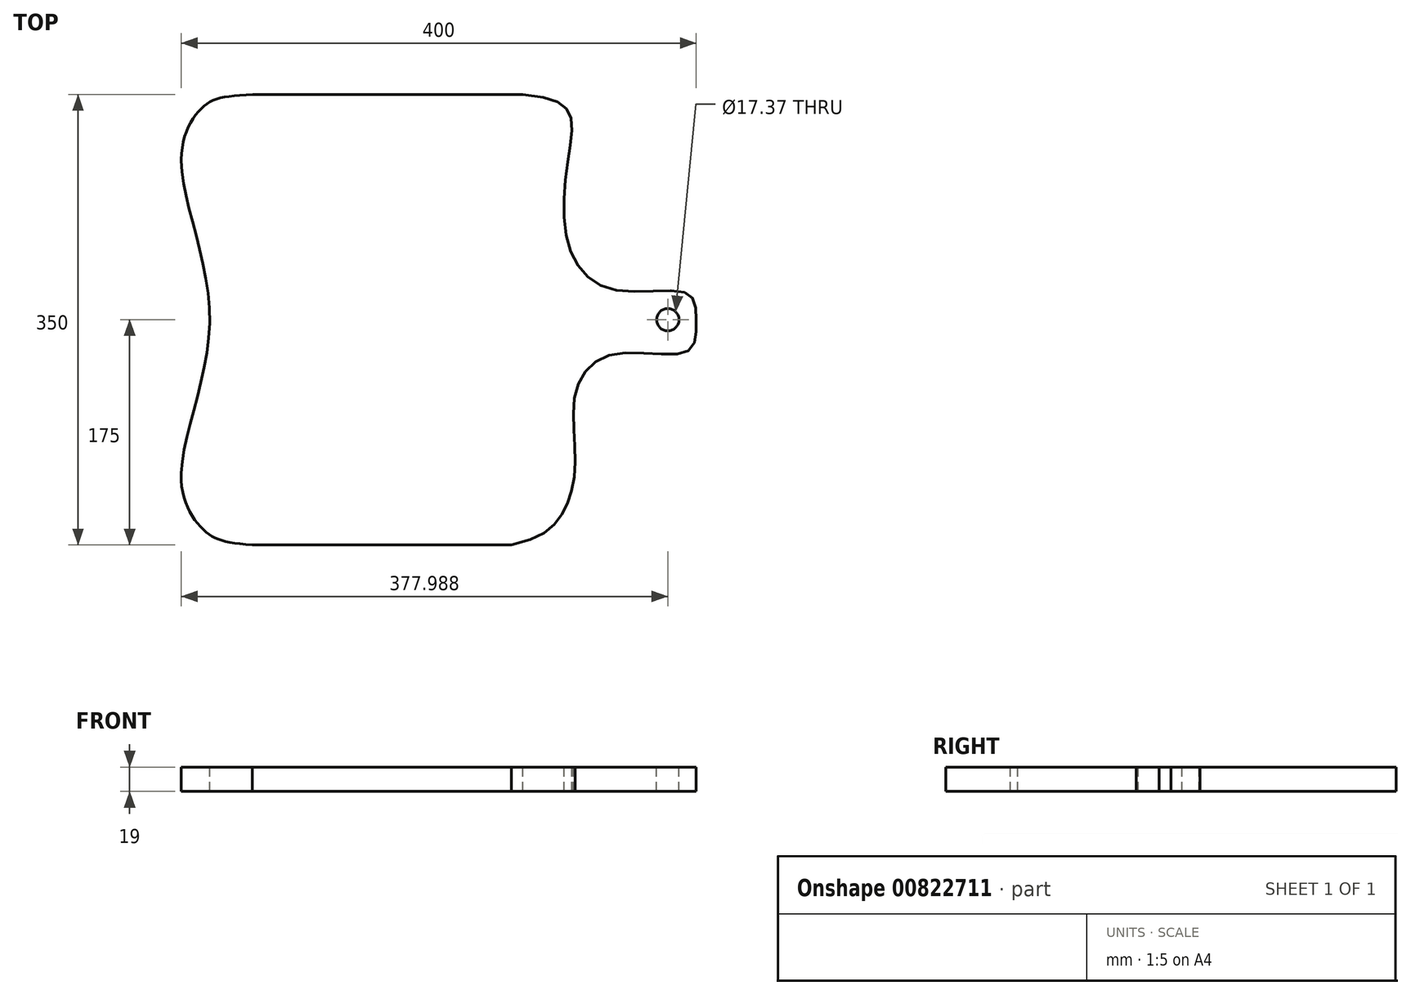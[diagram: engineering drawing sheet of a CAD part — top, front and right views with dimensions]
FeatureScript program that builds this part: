
annotation { "Feature Type Name" : "Feature", "Feature Type Description" : "" }
export const myFeature = defineFeature(function(context is Context, id is Id, definition is map)
    precondition{}
    {
        {
            var Q0;
            Q0=qCreatedBy(makeId("Top.planeOp"),FACE);
            var sketch = newSketch(context, id + "F0", { "sketchPlane" : qUnion([Q0])});
            skLineSegment(sketch, "E0.bottom", {"start": v(200, -175) * mm, "end": v(-200, -175) * mm});
            skLineSegment(sketch, "E0.top", {"start": v(200, 175) * mm, "end": v(-200, 175) * mm});
            skLineSegment(sketch, "E0.left", {"start": v(200, -175) * mm, "end": v(200, 175) * mm});
            skLineSegment(sketch, "E0.right", {"start": v(-200, -175) * mm, "end": v(-200, 175) * mm});
            skPoint(sketch, "E0.middle", {"position": v(0, 0) * mm});
            skSolve(sketch);
        }
        {
            var Q0;
            Q0 = qSketchRegion(id + "F0", true);
            extrude(context, id + "F1", {"entities" : qUnion([Q0]), "depth" : 19 * mm, "offsetDistance" : 25 * mm});
        }
        {
            var Q0;
            Q0=makeQuery(id+"F1.opExtrude","CAP_FACE",FACE,{"disambiguationData":[OSD([sQuery(id+"F0.wireOp",EDGE,"E0.bottom"),sQuery(id+"F0.wireOp",EDGE,"E0.top"),sQuery(id+"F0.wireOp",EDGE,"E0.left"),sQuery(id+"F0.wireOp",EDGE,"E0.right")])],"isStart":false});
            var sketch = newSketch(context, id + "F2", { "sketchPlane" : qUnion([Q0])});
            skFitSpline(sketch, "E1", {"points": [v(-144.39, 175) * mm, v(-182.7, 165.66) * mm, v(-200, 124.44) * mm, v(-177.97, 0) * mm, v(-200, -124.84) * mm, v(-180.58, -165.08) * mm, v(-144.98, -175) * mm, v(56.37, -175) * mm, v(96.18, -150.44) * mm, v(106.15, -110.63) * mm, v(106.57, -55.5) * mm, v(137.18, -26.5) * mm, v(193.56, -24.36) * mm, v(200, 0) * mm, v(193.56, 20.21) * mm, v(138.25, 22.9) * mm, v(103.09, 51.7) * mm, v(99.33, 116.14) * mm, v(101.98, 159.48) * mm, v(65.34, 175) * mm, v(-144.39, 175) * mm]});
            skCircle(sketch, "E2", {"center": v(177.99, 0) * mm, "radius": 8.68 * mm});
            skSolve(sketch);
        }
        {
            var Q0;
            {var subQ0=sQuery(id+"F2.wireOp",EDGE,"E1");var subQ1=makeQuery(id+"F1.opExtrude","CAP_EDGE",EDGE,{"disambiguationData":[OSD([sQuery(id+"F0.wireOp",EDGE,"E0.right")])],"isStart":false});var subQ2=makeQuery(id+"F2.imprint","INTERSECT",VERTEX,{"disambiguationData":[OD(1.0)],"derivedFrom":[subQ1,subQ0]});Q0=makeQuery(id+"F2.imprint","IMPRINT",FACE,{"disambiguationData":[TD([[makeQuery(id+"F2.imprint","IMPRINT",EDGE,{"disambiguationData":[TD([[subQ2,-1.0]])],"derivedFrom":subQ0}),-1.0]])]});}
            var Q1;
            {var subQ0=sQuery(id+"F2.wireOp",EDGE,"E1");var subQ1=makeQuery(id+"F1.opExtrude","CAP_EDGE",EDGE,{"disambiguationData":[OSD([sQuery(id+"F0.wireOp",EDGE,"E0.right")])],"isStart":false});var subQ2=makeQuery(id+"F2.imprint","INTERSECT",VERTEX,{"disambiguationData":[OD(0.0)],"derivedFrom":[subQ1,subQ0]});Q1=makeQuery(id+"F2.imprint","IMPRINT",FACE,{"disambiguationData":[TD([[makeQuery(id+"F2.imprint","IMPRINT",EDGE,{"disambiguationData":[TD([[subQ2,1.0]])],"derivedFrom":subQ0}),-1.0]])]});}
            var Q2;
            {var subQ0=sQuery(id+"F2.wireOp",EDGE,"E1");var subQ1=makeQuery(id+"F1.opExtrude","CAP_EDGE",EDGE,{"disambiguationData":[OSD([sQuery(id+"F0.wireOp",EDGE,"E0.right")])],"isStart":false});var subQ2=makeQuery(id+"F2.imprint","INTERSECT",VERTEX,{"disambiguationData":[OD(3.0)],"derivedFrom":[subQ1,subQ0]});Q2=makeQuery(id+"F2.imprint","IMPRINT",FACE,{"disambiguationData":[TD([[makeQuery(id+"F2.imprint","IMPRINT",EDGE,{"disambiguationData":[TD([[subQ2,-1.0]])],"derivedFrom":subQ0}),-1.0]])]});}
            var Q3;
            {var subQ0=sQuery(id+"F2.wireOp",EDGE,"E1");var subQ1=makeQuery(id+"F1.opExtrude","CAP_EDGE",EDGE,{"disambiguationData":[OSD([sQuery(id+"F0.wireOp",EDGE,"E0.bottom")])],"isStart":false});var subQ2=makeQuery(id+"F2.imprint","INTERSECT",VERTEX,{"disambiguationData":[OD(1.0)],"derivedFrom":[subQ1,subQ0]});Q3=makeQuery(id+"F2.imprint","IMPRINT",FACE,{"disambiguationData":[TD([[makeQuery(id+"F2.imprint","IMPRINT",EDGE,{"disambiguationData":[TD([[subQ2,-1.0]])],"derivedFrom":subQ0}),-1.0]])]});}
            var Q4;
            {var subQ0=sQuery(id+"F2.wireOp",EDGE,"E1");var subQ1=makeQuery(id+"F1.opExtrude","CAP_EDGE",EDGE,{"disambiguationData":[OSD([sQuery(id+"F0.wireOp",EDGE,"E0.left")])],"isStart":false});var subQ2=makeQuery(id+"F2.imprint","INTERSECT",VERTEX,{"disambiguationData":[OD(1.0)],"derivedFrom":[subQ1,subQ0]});Q4=makeQuery(id+"F2.imprint","IMPRINT",FACE,{"disambiguationData":[TD([[makeQuery(id+"F2.imprint","IMPRINT",EDGE,{"disambiguationData":[TD([[subQ2,-1.0]])],"derivedFrom":subQ0}),-1.0]])]});}
            extrude(context, id + "F3", {"entities" : qUnion([Q0, Q1, Q2, Q3, Q4]), "operationType" : NewBodyOperationType.REMOVE, "endBound" : BoundingType.THROUGH_ALL, "oppositeDirection" : true, "depth" : 25 * mm, "offsetDistance" : 25 * mm});
        }
        {
            var Q0;
            Q0=makeQuery(id+"F2.imprint","IMPRINT",FACE,{"disambiguationData":[TD([[makeQuery(id+"F2.imprint","IMPRINT",EDGE,{"derivedFrom":sQuery(id+"F2.wireOp",EDGE,"E2")}),1.0]])]});
            extrude(context, id + "F4", {"entities" : qUnion([Q0]), "operationType" : NewBodyOperationType.REMOVE, "endBound" : BoundingType.THROUGH_ALL, "oppositeDirection" : true, "depth" : 25 * mm, "offsetDistance" : 25 * mm});
        }
    });
